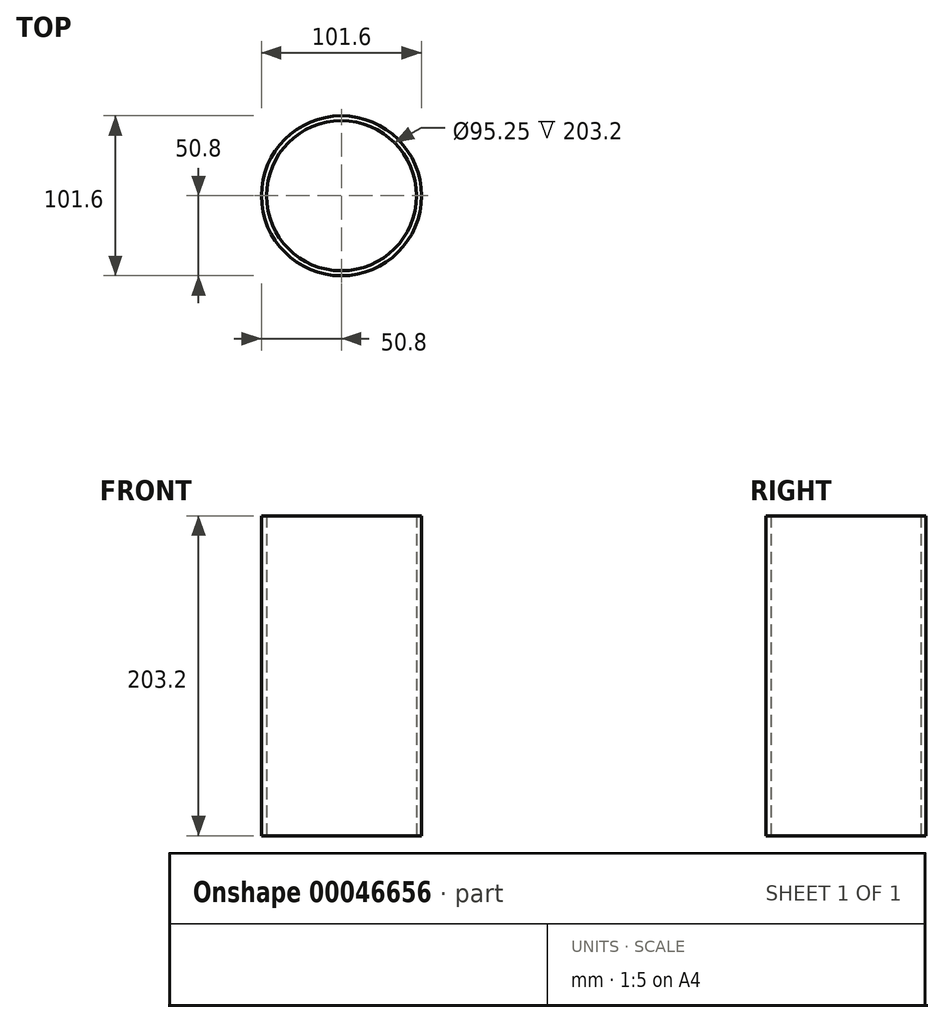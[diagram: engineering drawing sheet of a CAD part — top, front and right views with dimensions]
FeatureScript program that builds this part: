
annotation { "Feature Type Name" : "Feature", "Feature Type Description" : "" }
export const myFeature = defineFeature(function(context is Context, id is Id, definition is map)
    precondition{}
    {
        {
            var Q0;
            Q0=qCreatedBy(makeId("Top.planeOp"),FACE);
            var sketch = newSketch(context, id + "F0", { "sketchPlane" : qUnion([Q0])});
            skCircle(sketch, "E0", {"center": v(0, 0) * mm, "radius": 50.8 * mm});
            skCircle(sketch, "E1", {"center": v(0, 0) * mm, "radius": 47.63 * mm});
            skSolve(sketch);
        }
        {
            var Q0;
            Q0 = qSketchRegion(id + "F0", true);
            extrude(context, id + "F1", {"entities" : qUnion([Q0]), "depth" : 203.2 * mm});
        }
    });
